FCSTD DOCUMENT  (FreeCAD 0.20R29603 (Git))
Label: DeskAssembly
License: All rights reserved
LicenseURL: http://en.wikipedia.org/wiki/All_rights_reserved
objects: App::Link×17, App::DocumentObjectGroup×3, PartDesign::CoordinateSystem×1, App::FeaturePython×1, App::Part×1
note: 1 computed .brp shape members not serialized (recipe doc carries the construction recipe); baked Part::Feature solids carry a one-line shape summary decoded from their .brp
EXTERNAL_REF file=Desktop.FCStd obj=Model
EXTERNAL_REF file=Parameters.FCStd obj=Spreadsheet
EXTERNAL_REF file=Leg.FCStd obj=Model
EXTERNAL_REF file=LongSkirt.FCStd obj=Model
EXTERNAL_REF file=ShortSkirt.FCStd obj=Model
EXTERNAL_REF file=LegSpacer.FCStd obj=Model

FEATURE [App::DocumentObjectGroup] Parts
FEATURE [PartDesign::CoordinateSystem] LCS_Origin
  AttacherType = Attacher::AttachEngine3D
  MapMode = 2
  Support = -> [X_Axis]
FEATURE [App::DocumentObjectGroup] Constraints
FEATURE [App::FeaturePython] Variables  # WARN: FeaturePython — macro-defined, semantics opaque (R4)
  Type = App::PropertyContainer
FEATURE [App::DocumentObjectGroup] Configurations
FEATURE [App::Link] DeskTop
  AttachedBy = #LCS_Origin
  AttachedTo = Parent Assembly#LCS_Origin
  LinkedObject = -> <external Desktop.FCStd>#Model
FEATURE [App::Link] NorthEastLegA
  AttachedBy = #LCS_Origin
  AttachedTo = Parent Assembly#LCS_Origin
  AttachmentOffset = pos=(0,0,0) rot=(-0.57735,-0.57735,0.57735;4.18879rad)
  LinkPlacement = pos=(-609.6,-286.941,0) rot=(-0.57735,-0.57735,0.57735;4.18879rad)
  LinkedObject = -> <external Leg.FCStd>#Model
  Placement = pos=(-609.6,-286.941,0) rot=(-0.57735,-0.57735,0.57735;4.18879rad)
  expr: .Placement.Base.x = -<<Parameters>>#<<DeskDimensions>>.Skirt_Length / 2
  expr: .Placement.Base.y = -<<Parameters>>#<<DeskDimensions>>.Skirt_Width / 2
FEATURE [App::Link] NorthEastLegB
  AttachedBy = #LCS_Origin
  AttachedTo = Parent Assembly#LCS_Origin
  AttachmentOffset = pos=(0,0,0) rot=(-0.57735,-0.57735,0.57735;4.18879rad)
  LinkPlacement = pos=(-609.6,-310.753,0) rot=(-0.57735,-0.57735,0.57735;4.18879rad)
  LinkedObject = -> <external Leg.FCStd>#Model
  Placement = pos=(-609.6,-310.753,0) rot=(-0.57735,-0.57735,0.57735;4.18879rad)
  expr: .Placement.Base.x = -<<Parameters>>#<<DeskDimensions>>.Skirt_Length / 2
  expr: .Placement.Base.y = -<<Parameters>>#<<DeskDimensions>>.Skirt_Width / 2 - 2 * Parameters#<<DeskDimensions>>.Stock_Thickness
FEATURE [App::Link] NorthWestLegA
  AttachedBy = #LCS_Origin
  AttachedTo = Parent Assembly#LCS_Origin
  AttachmentOffset = pos=(0,0,0) rot=(-0.57735,-0.57735,0.57735;4.18879rad)
  LinkPlacement = pos=(-609.6,298.847,0) rot=(-0.57735,-0.57735,0.57735;4.18879rad)
  LinkedObject = -> <external Leg.FCStd>#Model
  Placement = pos=(-609.6,298.847,0) rot=(-0.57735,-0.57735,0.57735;4.18879rad)
  expr: .Placement.Base.x = -<<Parameters>>#<<DeskDimensions>>.Skirt_Length / 2
  expr: .Placement.Base.y = <<Parameters>>#<<DeskDimensions>>.Skirt_Width / 2 + Parameters#<<DeskDimensions>>.Stock_Thickness
FEATURE [App::Link] NorthWestLegB
  AttachedBy = #LCS_Origin
  AttachedTo = Parent Assembly#LCS_Origin
  AttachmentOffset = pos=(0,0,0) rot=(-0.57735,-0.57735,0.57735;4.18879rad)
  LinkPlacement = pos=(-609.6,322.659,0) rot=(-0.57735,-0.57735,0.57735;4.18879rad)
  LinkedObject = -> <external Leg.FCStd>#Model
  Placement = pos=(-609.6,322.659,0) rot=(-0.57735,-0.57735,0.57735;4.18879rad)
  expr: .Placement.Base.x = -<<Parameters>>#<<DeskDimensions>>.Skirt_Length / 2
  expr: .Placement.Base.y = <<Parameters>>#<<DeskDimensions>>.Skirt_Width / 2 + 3 * Parameters#<<DeskDimensions>>.Stock_Thickness
FEATURE [App::Link] SouthLongSkirt
  AttachedBy = #LCS_Origin
  AttachedTo = Parent Assembly#LCS_Origin
  AttachmentOffset = pos=(0,0,0) rot=(1,0,0;1.5708rad)
  LinkPlacement = pos=(0,310.753,0) rot=(1,0,0;1.5708rad)
  LinkedObject = -> <external LongSkirt.FCStd>#Model
  Placement = pos=(0,310.753,0) rot=(1,0,0;1.5708rad)
  expr: .Placement.Base.y = Parameters#<<DeskDimensions>>.Skirt_Width / 2 + 2 * Parameters#<<DeskDimensions>>.Stock_Thickness
FEATURE [App::Link] NorthLongSkirt
  AttachedBy = #LCS_Origin
  AttachedTo = Parent Assembly#LCS_Origin
  AttachmentOffset = pos=(0,0,0) rot=(1,0,0;1.5708rad)
  LinkPlacement = pos=(0,-298.847,0) rot=(1,0,0;1.5708rad)
  LinkedObject = -> <external LongSkirt.FCStd>#Model
  Placement = pos=(0,-298.847,0) rot=(1,0,0;1.5708rad)
  expr: .Placement.Base.y = -Parameters#<<DeskDimensions>>.Skirt_Width / 2 - Parameters#<<DeskDimensions>>.Stock_Thickness
FEATURE [App::Link] EastShortSkirt
  AttachedBy = #LCS_Origin
  AttachedTo = Parent Assembly#LCS_Origin
  AttachmentOffset = pos=(0,0,0) rot=(-0.57735,0.57735,0.57735;4.18879rad)
  LinkPlacement = pos=(609.6,0,0) rot=(-0.57735,0.57735,0.57735;4.18879rad)
  LinkedObject = -> <external ShortSkirt.FCStd>#Model
  Placement = pos=(609.6,0,0) rot=(-0.57735,0.57735,0.57735;4.18879rad)
  expr: .Placement.Base.x = Parameters#<<DeskDimensions>>.Skirt_Length / 2
FEATURE [App::Link] WestShortSkirt
  AttachedBy = #LCS_Origin
  AttachedTo = Parent Assembly#LCS_Origin
  AttachmentOffset = pos=(0,0,0) rot=(0.57735,0.57735,0.57735;2.0944rad)
  LinkPlacement = pos=(-609.6,0,0) rot=(0.57735,0.57735,0.57735;2.0944rad)
  LinkedObject = -> <external ShortSkirt.FCStd>#Model
  Placement = pos=(-609.6,0,0) rot=(0.57735,0.57735,0.57735;2.0944rad)
  expr: .Placement.Base.x = -Parameters#<<DeskDimensions>>.Skirt_Length / 2
FEATURE [App::Link] SoutEastLegA
  AttachedBy = #LCS_Origin
  AttachedTo = Parent Assembly#LCS_Origin
  AttachmentOffset = pos=(0,0,0) rot=(0.57735,-0.57735,-0.57735;4.18879rad)
  LinkPlacement = pos=(609.6,-298.847,0) rot=(0.57735,-0.57735,-0.57735;4.18879rad)
  LinkedObject = -> <external Leg.FCStd>#Model
  Placement = pos=(609.6,-298.847,0) rot=(0.57735,-0.57735,-0.57735;4.18879rad)
  expr: .Placement.Base.x = <<Parameters>>#<<DeskDimensions>>.Skirt_Length / 2
  expr: .Placement.Base.y = -<<Parameters>>#<<DeskDimensions>>.Skirt_Width / 2 - Parameters#<<DeskDimensions>>.Stock_Thickness
FEATURE [App::Link] SoutEastLegB
  AttachedBy = #LCS_Origin
  AttachedTo = Parent Assembly#LCS_Origin
  AttachmentOffset = pos=(0,0,0) rot=(0.57735,-0.57735,-0.57735;4.18879rad)
  LinkPlacement = pos=(609.6,-322.659,0) rot=(0.57735,-0.57735,-0.57735;4.18879rad)
  LinkedObject = -> <external Leg.FCStd>#Model
  Placement = pos=(609.6,-322.659,0) rot=(0.57735,-0.57735,-0.57735;4.18879rad)
  expr: .Placement.Base.x = <<Parameters>>#<<DeskDimensions>>.Skirt_Length / 2
  expr: .Placement.Base.y = -<<Parameters>>#<<DeskDimensions>>.Skirt_Width / 2 - 3 * Parameters#<<DeskDimensions>>.Stock_Thickness
FEATURE [App::Link] SoutWestLegA
  AttachedBy = #LCS_Origin
  AttachedTo = Parent Assembly#LCS_Origin
  AttachmentOffset = pos=(0,0,0) rot=(0.57735,-0.57735,-0.57735;4.18879rad)
  LinkPlacement = pos=(609.6,310.753,0) rot=(0.57735,-0.57735,-0.57735;4.18879rad)
  LinkedObject = -> <external Leg.FCStd>#Model
  Placement = pos=(609.6,310.753,0) rot=(0.57735,-0.57735,-0.57735;4.18879rad)
  expr: .Placement.Base.x = <<Parameters>>#<<DeskDimensions>>.Skirt_Length / 2
  expr: .Placement.Base.y = <<Parameters>>#<<DeskDimensions>>.Skirt_Width / 2 + 2 * Parameters#<<DeskDimensions>>.Stock_Thickness
FEATURE [App::Link] SoutWestLegB
  AttachedBy = #LCS_Origin
  AttachedTo = Parent Assembly#LCS_Origin
  AttachmentOffset = pos=(0,0,0) rot=(0.57735,-0.57735,-0.57735;4.18879rad)
  LinkPlacement = pos=(609.6,286.941,0) rot=(0.57735,-0.57735,-0.57735;4.18879rad)
  LinkedObject = -> <external Leg.FCStd>#Model
  Placement = pos=(609.6,286.941,0) rot=(0.57735,-0.57735,-0.57735;4.18879rad)
  expr: .Placement.Base.x = <<Parameters>>#<<DeskDimensions>>.Skirt_Length / 2
  expr: .Placement.Base.y = <<Parameters>>#<<DeskDimensions>>.Skirt_Width / 2
FEATURE [App::Link] NorthEastLegSpacer
  AttachedBy = #LCS_Origin
  AttachedTo = Parent Assembly#LCS_Origin
  AttachmentOffset = pos=(0,0,0) rot=(-0.57735,-0.57735,0.57735;4.18879rad)
  LinkPlacement = pos=(-609.6,-298.847,0) rot=(-0.57735,-0.57735,0.57735;4.18879rad)
  LinkedObject = -> <external LegSpacer.FCStd>#Model
  Placement = pos=(-609.6,-298.847,0) rot=(-0.57735,-0.57735,0.57735;4.18879rad)
  expr: .Placement.Base.x = -<<Parameters>>#<<DeskDimensions>>.Skirt_Length / 2
  expr: .Placement.Base.y = -<<Parameters>>#<<DeskDimensions>>.Skirt_Width / 2 - <<Parameters>>#<<DeskDimensions>>.Stock_Thickness
FEATURE [App::Link] NorthWestLegSpacer
  AttachedBy = #LCS_Origin
  AttachedTo = Parent Assembly#LCS_Origin
  AttachmentOffset = pos=(0,0,0) rot=(-0.57735,-0.57735,0.57735;4.18879rad)
  LinkPlacement = pos=(-609.6,310.753,0) rot=(-0.57735,-0.57735,0.57735;4.18879rad)
  LinkedObject = -> <external LegSpacer.FCStd>#Model
  Placement = pos=(-609.6,310.753,0) rot=(-0.57735,-0.57735,0.57735;4.18879rad)
  expr: .Placement.Base.x = -<<Parameters>>#<<DeskDimensions>>.Skirt_Length / 2
  expr: .Placement.Base.y = <<Parameters>>#<<DeskDimensions>>.Skirt_Width / 2 + 2 * Parameters#<<DeskDimensions>>.Stock_Thickness
FEATURE [App::Link] SouthEastLegSpacer
  AttachedBy = #LCS_Origin
  AttachedTo = Parent Assembly#LCS_Origin
  AttachmentOffset = pos=(0,0,0) rot=(0.57735,-0.57735,-0.57735;4.18879rad)
  LinkPlacement = pos=(609.6,-310.753,0) rot=(0.57735,-0.57735,-0.57735;4.18879rad)
  LinkedObject = -> <external LegSpacer.FCStd>#Model
  Placement = pos=(609.6,-310.753,0) rot=(0.57735,-0.57735,-0.57735;4.18879rad)
  expr: .Placement.Base.x = <<Parameters>>#<<DeskDimensions>>.Skirt_Length / 2
  expr: .Placement.Base.y = -<<Parameters>>#<<DeskDimensions>>.Skirt_Width / 2 - 2 * Parameters#<<DeskDimensions>>.Stock_Thickness
FEATURE [App::Link] SouthWestLegSpacer
  AttachedBy = #LCS_Origin
  AttachedTo = Parent Assembly#LCS_Origin
  AttachmentOffset = pos=(0,0,0) rot=(0.57735,-0.57735,-0.57735;4.18879rad)
  LinkPlacement = pos=(609.6,298.847,0) rot=(0.57735,-0.57735,-0.57735;4.18879rad)
  LinkedObject = -> <external LegSpacer.FCStd>#Model
  Placement = pos=(609.6,298.847,0) rot=(0.57735,-0.57735,-0.57735;4.18879rad)
  expr: .Placement.Base.x = <<Parameters>>#<<DeskDimensions>>.Skirt_Length / 2
  expr: .Placement.Base.y = <<Parameters>>#<<DeskDimensions>>.Skirt_Width / 2 + Parameters#<<DeskDimensions>>.Stock_Thickness
FEATURE [App::Part] Model
  AssemblyType = Part::Link
  Group = -> [LCS_Origin,Constraints,Variables,Configurations,DeskTop,NorthEastLegA,NorthEastLegB,NorthWestLegA,NorthWestLegB,SouthLongSkirt,NorthLongSkirt,EastShortSkirt,WestShortSkirt,SoutEastLegA,SoutEastLegB,SoutWestLegA,SoutWestLegB,NorthEastLegSpacer,NorthWestLegSpacer,SouthEastLegSpacer,SouthWestLegSpacer]
  Origin = -> Origin
  Type = Assembly

RESOLVED EXTERNAL PARTS (link-assembly join: the EXTERNAL_REF files above that resolve inside this repo's crawl, each included once):
---- part Desktop.FCStd = doc fcstd_15b475320501 ----
FCSTD DOCUMENT  (FreeCAD 0.20R29603 (Git))
Label: Desktop
License: All rights reserved
LicenseURL: http://en.wikipedia.org/wiki/All_rights_reserved
objects: App::DocumentObjectGroup×3, Sketcher::SketchObject×1, PartDesign::Pad×1, PartDesign::Body×1, PartDesign::CoordinateSystem×1, App::FeaturePython×1, App::Part×1
note: 5 computed .brp shape members not serialized (recipe doc carries the construction recipe); baked Part::Feature solids carry a one-line shape summary decoded from their .brp
EXTERNAL_REF file=Parameters.FCStd obj=Spreadsheet

FEATURE [Sketcher::SketchObject] Sketch
  FullyConstrained = true
  MapMode = 5
  Support = -> [XY_Plane]
  expr: Constraints[8] = <<Parameters>>#<<DeskDimensions>>.Table_Length
  expr: Constraints[9] = <<Parameters>>#<<DeskDimensions>>.Table_Width
  sketch-geometry (4):
    g0: LineSegment StartX=-685.8 StartY=381 StartZ=0 EndX=685.8 EndY=381 EndZ=0
    g1: LineSegment StartX=685.8 StartY=381 StartZ=0 EndX=685.8 EndY=-381 EndZ=0
    g2: LineSegment StartX=685.8 StartY=-381 StartZ=0 EndX=-685.8 EndY=-381 EndZ=0
    g3: LineSegment StartX=-685.8 StartY=-381 StartZ=0 EndX=-685.8 EndY=381 EndZ=0
  constraints (11):
    c: Coincident(g0,g1)
    c: Coincident(g1,g2)
    c: Coincident(g2,g3)
    c: Coincident(g3,g0)
    c: Horizontal(g0)
    c: Horizontal(g2)
    c: Vertical(g1)
    c: Vertical(g3)
    c: DistanceX(g0,g0) = 1371.6
    c: DistanceY(g3,g3) = 762
    c: Symmetric(g0,g1,g-1)
FEATURE [PartDesign::Pad] Pad
  Direction = (0,0,1)
  Length = 11.9062
  Length2 = 10
  Profile = -> Sketch
  ReferenceAxis = -> Sketch [N_Axis]
  Type = 0
  expr: Length = <<Parameters>>#<<DeskDimensions>>.Stock_Thickness
FEATURE [PartDesign::Body] Body
  Group = -> [Sketch,Pad]
  Origin = -> Origin
  Tip = -> Pad
FEATURE [App::DocumentObjectGroup] Parts
FEATURE [PartDesign::CoordinateSystem] LCS_Origin
  AttacherType = Attacher::AttachEngine3D
  MapMode = 2
  Support = -> [X_Axis001]
FEATURE [App::DocumentObjectGroup] Constraints
FEATURE [App::FeaturePython] Variables  # WARN: FeaturePython — macro-defined, semantics opaque (R4)
  Type = App::PropertyContainer
FEATURE [App::DocumentObjectGroup] Configurations
FEATURE [App::Part] Model
  AssemblyType = Part::Link
  Group = -> [LCS_Origin,Constraints,Variables,Configurations,Body]
  Origin = -> Origin001
  SolverId = Asm4EE
  Type = Assembly
---- part Leg.FCStd = doc fcstd_bca13a922b1c ----
FCSTD DOCUMENT  (FreeCAD 0.20R29603 (Git))
Label: Leg
License: All rights reserved
LicenseURL: http://en.wikipedia.org/wiki/All_rights_reserved
objects: App::DocumentObjectGroup×3, Sketcher::SketchObject×1, PartDesign::Pad×1, PartDesign::Body×1, PartDesign::CoordinateSystem×1, App::FeaturePython×1, App::Part×1
note: 5 computed .brp shape members not serialized (recipe doc carries the construction recipe); baked Part::Feature solids carry a one-line shape summary decoded from their .brp
EXTERNAL_REF file=Parameters.FCStd obj=Spreadsheet

FEATURE [Sketcher::SketchObject] Sketch
  FullyConstrained = false
  MapMode = 5
  Support = -> [XY_Plane]
  expr: Constraints[10] = <<Parameters>>#<<DeskDimensions>>.Leg_Top
  expr: Constraints[16] = <<Parameters>>#<<DeskDimensions>>.Leg_Bottom
  expr: Constraints[5] = <<Parameters>>#<<DeskDimensions>>.Leg_Length
  sketch-geometry (8):
    g0: LineSegment StartX=0 StartY=114.3 StartZ=0 EndX=0 EndY=0 EndZ=0
    g1: LineSegment StartX=0 StartY=0 StartZ=0 EndX=762 EndY=-107.092 EndZ=0
    g2: LineSegment StartX=0 StartY=-107.092 StartZ=0 EndX=762 EndY=-107.092 EndZ=0
    g3: LineSegment StartX=762 StartY=-107.092 StartZ=0 EndX=762 EndY=534.568 EndZ=0
    g4: LineSegment StartX=762 StartY=534.568 StartZ=0 EndX=0 EndY=534.568 EndZ=0
    g5: LineSegment StartX=0 StartY=534.568 StartZ=0 EndX=0 EndY=-107.092 EndZ=0
    g6: LineSegment StartX=762 StartY=-107.092 StartZ=0 EndX=762 EndY=-56.2921 EndZ=0
    g7: LineSegment StartX=762 StartY=-56.2921 StartZ=0 EndX=0 EndY=114.3 EndZ=0
  constraints (22):
    c: Coincident(g4,g5)
    c: Coincident(g5,g2)
    c: Horizontal(g4)
    c: Vertical(g3)
    c: Vertical(g5)
    c: DistanceX(g4,g4) = 762
    c: Coincident(g1,g2)
    c: Angle(g1,g0) = 1.71042
    c: Horizontal(g2)
    c: Vertical(g0)
    c: DistanceY(g0,g0) = 114.3
    c: PointOnObject(g0,g5)
    c: Coincident(g6,g1)
    c: Vertical(g6)
    c: Coincident(g7,g6)
    c: Coincident(g7,g0)
    c: DistanceY(g6,g6) = 50.8
    c: Coincident(g3,g1)
    c: Coincident(g4,g3)
    c: Coincident(g1,g0)
    c: DistanceX(g0) = 0
    c: DistanceY(g0) = 0
FEATURE [PartDesign::Pad] Pad
  Direction = (0,0,1)
  Length = 11.9062
  Length2 = 10
  Profile = -> Sketch
  ReferenceAxis = -> Sketch [N_Axis]
  Type = 0
  expr: Length = <<Parameters>>#<<DeskDimensions>>.Stock_Thickness
FEATURE [PartDesign::Body] Body
  Group = -> [Sketch,Pad]
  Origin = -> Origin
  Tip = -> Pad
FEATURE [App::DocumentObjectGroup] Parts
FEATURE [PartDesign::CoordinateSystem] LCS_Origin
  AttacherType = Attacher::AttachEngine3D
  MapMode = 2
  Support = -> [X_Axis001]
FEATURE [App::DocumentObjectGroup] Constraints
FEATURE [App::FeaturePython] Variables  # WARN: FeaturePython — macro-defined, semantics opaque (R4)
  Type = App::PropertyContainer
FEATURE [App::DocumentObjectGroup] Configurations
FEATURE [App::Part] Model
  Group = -> [LCS_Origin,Constraints,Variables,Configurations,Body]
  Origin = -> Origin001
  Type = Assembly
---- part LegSpacer.FCStd = doc fcstd_51fb333a3f8a ----
FCSTD DOCUMENT  (FreeCAD 0.20R29603 (Git))
Label: LegSpacer
License: All rights reserved
LicenseURL: http://en.wikipedia.org/wiki/All_rights_reserved
objects: App::DocumentObjectGroup×3, Sketcher::SketchObject×2, PartDesign::Pad×1, PartDesign::CoordinateSystem×1, App::FeaturePython×1, PartDesign::Pocket×1, PartDesign::Body×1, App::Part×1
note: 8 computed .brp shape members not serialized (recipe doc carries the construction recipe); baked Part::Feature solids carry a one-line shape summary decoded from their .brp
EXTERNAL_REF file=Parameters.FCStd obj=Spreadsheet

FEATURE [Sketcher::SketchObject] Sketch
  FullyConstrained = false
  MapMode = 5
  Support = -> [XY_Plane]
  expr: Constraints[10] = <<Parameters>>#<<DeskDimensions>>.Leg_Top
  expr: Constraints[16] = <<Parameters>>#<<DeskDimensions>>.Leg_Bottom
  expr: Constraints[5] = <<Parameters>>#<<DeskDimensions>>.Leg_Length
  sketch-geometry (8):
    g0: LineSegment StartX=0 StartY=114.3 StartZ=0 EndX=0 EndY=0 EndZ=0
    g1: LineSegment StartX=0 StartY=0 StartZ=0 EndX=762 EndY=-107.092 EndZ=0
    g2: LineSegment StartX=0 StartY=-107.092 StartZ=0 EndX=762 EndY=-107.092 EndZ=0
    g3: LineSegment StartX=762 StartY=-107.092 StartZ=0 EndX=762 EndY=534.568 EndZ=0
    g4: LineSegment StartX=762 StartY=534.568 StartZ=0 EndX=0 EndY=534.568 EndZ=0
    g5: LineSegment StartX=0 StartY=534.568 StartZ=0 EndX=0 EndY=-107.092 EndZ=0
    g6: LineSegment StartX=762 StartY=-107.092 StartZ=0 EndX=762 EndY=-56.2921 EndZ=0
    g7: LineSegment StartX=762 StartY=-56.2921 StartZ=0 EndX=0 EndY=114.3 EndZ=0
  constraints (22):
    c: Coincident(g4,g5)
    c: Coincident(g5,g2)
    c: Horizontal(g4)
    c: Vertical(g3)
    c: Vertical(g5)
    c: DistanceX(g4,g4) = 762
    c: Coincident(g1,g2)
    c: Angle(g1,g0) = 1.71042
    c: Horizontal(g2)
    c: Vertical(g0)
    c: DistanceY(g0,g0) = 114.3
    c: PointOnObject(g0,g5)
    c: Coincident(g6,g1)
    c: Vertical(g6)
    c: Coincident(g7,g6)
    c: Coincident(g7,g0)
    c: DistanceY(g6,g6) = 50.8
    c: Coincident(g3,g1)
    c: Coincident(g4,g3)
    c: Coincident(g1,g0)
    c: DistanceX(g0) = 0
    c: DistanceY(g0) = 0
FEATURE [PartDesign::Pad] Pad
  Direction = (0,0,1)
  Length = 11.9062
  Length2 = 10
  Profile = -> Sketch
  ReferenceAxis = -> Sketch [N_Axis]
  Type = 0
  expr: Length = <<Parameters>>#<<DeskDimensions>>.Stock_Thickness
FEATURE [App::DocumentObjectGroup] Parts
FEATURE [PartDesign::CoordinateSystem] LCS_Origin
  AttacherType = Attacher::AttachEngine3D
  MapMode = 2
  Support = -> [X_Axis001]
FEATURE [App::DocumentObjectGroup] Constraints
FEATURE [App::FeaturePython] Variables  # WARN: FeaturePython — macro-defined, semantics opaque (R4)
  Type = App::PropertyContainer
FEATURE [App::DocumentObjectGroup] Configurations
FEATURE [Sketcher::SketchObject] Sketch001
  AttachmentOffset = pos=(0,0,11.9062) rot=(0,0,1;0rad)
  FullyConstrained = true
  MapMode = 5
  Placement = pos=(0,0,11.9062) rot=(0,0,1;0rad)
  Support = -> [XY_Plane]
  expr: .AttachmentOffset.Base.z = Parameters#<<DeskDimensions>>.Stock_Thickness
  expr: Constraints[8] = Parameters#<<DeskDimensions>>.Leg_Length - 2"
  expr: Constraints[9] = Parameters#<<DeskDimensions>>.Table_Length
  sketch-geometry (4):
    g0: LineSegment StartX=0 StartY=685.8 StartZ=0 EndX=711.2 EndY=685.8 EndZ=0
    g1: LineSegment StartX=711.2 StartY=685.8 StartZ=0 EndX=711.2 EndY=-685.8 EndZ=0
    g2: LineSegment StartX=711.2 StartY=-685.8 StartZ=0 EndX=0 EndY=-685.8 EndZ=0
    g3: LineSegment StartX=0 StartY=-685.8 StartZ=0 EndX=0 EndY=685.8 EndZ=0
  constraints (11):
    c: Coincident(g0,g1)
    c: Coincident(g1,g2)
    c: Coincident(g2,g3)
    c: Coincident(g3,g0)
    c: Horizontal(g0)
    c: Horizontal(g2)
    c: Vertical(g1)
    c: Vertical(g3)
    c: DistanceX(g0,g0) = 711.2
    c: DistanceY(g3,g3) = 1371.6
    c: Symmetric(g2,g0,g-1)
FEATURE [PartDesign::Pocket] Pocket
  BaseFeature = -> Pad
  Direction = (0,0,-1)
  Length = 11.9062
  Length2 = 5
  Profile = -> Sketch001
  ReferenceAxis = -> Sketch001 [N_Axis]
  Type = 0
  expr: Length = Parameters#<<DeskDimensions>>.Stock_Thickness
FEATURE [PartDesign::Body] Body
  Group = -> [Sketch,Pad,Sketch001,Pocket]
  Origin = -> Origin
  Tip = -> Pocket
FEATURE [App::Part] Model
  Group = -> [LCS_Origin,Constraints,Variables,Configurations,Body]
  Origin = -> Origin001
  Type = Assembly
---- part LongSkirt.FCStd = doc fcstd_8dcfb7d38782 ----
FCSTD DOCUMENT  (FreeCAD 0.20R29603 (Git))
Label: LongSkirt
License: All rights reserved
LicenseURL: http://en.wikipedia.org/wiki/All_rights_reserved
objects: App::DocumentObjectGroup×3, Sketcher::SketchObject×1, PartDesign::Pad×1, PartDesign::Body×1, PartDesign::CoordinateSystem×1, App::FeaturePython×1, App::Part×1
note: 5 computed .brp shape members not serialized (recipe doc carries the construction recipe); baked Part::Feature solids carry a one-line shape summary decoded from their .brp
EXTERNAL_REF file=Parameters.FCStd obj=Spreadsheet

FEATURE [Sketcher::SketchObject] Sketch
  FullyConstrained = true
  MapMode = 5
  Support = -> [XY_Plane]
  expr: Constraints[17] = <<Parameters>>#<<DeskDimensions>>.Skirt_Length
  expr: Constraints[18] = <<Parameters>>#<<DeskDimensions>>.Skirt_Height
  expr: Constraints[3] = Parameters#<<DeskDimensions>>.Skirt_Length
  sketch-geometry (8):
    g0: LineSegment StartX=-609.6 StartY=0 StartZ=0 EndX=609.6 EndY=0 EndZ=0
    g1: LineSegment StartX=609.6 StartY=0 StartZ=0 EndX=623.879 EndY=-101.6 EndZ=0
    g2: LineSegment StartX=-623.879 StartY=-101.6 StartZ=0 EndX=-609.6 EndY=0 EndZ=0
    g3: LineSegment StartX=-623.879 StartY=-101.6 StartZ=0 EndX=623.879 EndY=-101.6 EndZ=0
    g4: LineSegment StartX=-609.6 StartY=0 StartZ=0 EndX=609.6 EndY=0 EndZ=0
    g5: LineSegment StartX=609.6 StartY=0 StartZ=0 EndX=609.6 EndY=-101.6 EndZ=0
    g6: LineSegment StartX=609.6 StartY=-101.6 StartZ=0 EndX=-609.6 EndY=-101.6 EndZ=0
    g7: LineSegment StartX=-609.6 StartY=-101.6 StartZ=0 EndX=-609.6 EndY=0 EndZ=0
  constraints (22):
    c: Coincident(g0,g1)
    c: Coincident(g2,g0)
    c: Horizontal(g0)
    c: DistanceX(g0,g0) = 1219.2
    c: Angle(g2,g0) = 1.71042
    c: Angle(g0,g1) = 1.71042
    c: Coincident(g3,g2)
    c: Coincident(g3,g1)
    c: Horizontal(g3)
    c: Coincident(g4,g5)
    c: Coincident(g5,g6)
    c: Coincident(g6,g7)
    c: Coincident(g7,g4)
    c: Horizontal(g4)
    c: Horizontal(g6)
    c: Vertical(g5)
    c: Vertical(g7)
    c: DistanceX(g4,g4) = 1219.2
    c: DistanceY(g5,g5) = 101.6
    c: Coincident(g0,g4)
    c: PointOnObject(g6,g3)
    c: Symmetric(g0,g0,g-1)
FEATURE [PartDesign::Pad] Pad
  Direction = (0,0,1)
  Length = 11.9062
  Length2 = 10
  Profile = -> Sketch
  ReferenceAxis = -> Sketch [N_Axis]
  Type = 0
  expr: Length = Parameters#<<DeskDimensions>>.Stock_Thickness
FEATURE [PartDesign::Body] Body
  Group = -> [Sketch,Pad]
  Origin = -> Origin
  Tip = -> Pad
FEATURE [App::DocumentObjectGroup] Parts
FEATURE [PartDesign::CoordinateSystem] LCS_Origin
  AttacherType = Attacher::AttachEngine3D
  MapMode = 2
  Support = -> [X_Axis001]
FEATURE [App::DocumentObjectGroup] Constraints
FEATURE [App::FeaturePython] Variables  # WARN: FeaturePython — macro-defined, semantics opaque (R4)
  Type = App::PropertyContainer
FEATURE [App::DocumentObjectGroup] Configurations
FEATURE [App::Part] Model
  Group = -> [LCS_Origin,Constraints,Variables,Configurations,Body]
  Origin = -> Origin001
  Type = Assembly
---- part Parameters.FCStd = doc fcstd_c83a1a0fdc62 ----
FCSTD DOCUMENT  (FreeCAD 0.20R29603 (Git))
Label: Parameters
License: All rights reserved
LicenseURL: http://en.wikipedia.org/wiki/All_rights_reserved
objects: Spreadsheet::Sheet×2

FEATURE [Spreadsheet::Sheet] Spreadsheet  label="DeskDimensions"
  cells = A1=Desk Parameters; A2=Stock Thickness; B2(Stock_Thickness)==15" / 32; A4=Table Width; B4(Table_Width)==2.5'; A5=Table Length; B5(Table_Length)==4.5'; A7=Leg Length; B7(Leg_Length)==30"; A8=Leg Top; B8(Leg_Top)==4.5"; A9=Leg Bottom; B9(Leg_Bottom)==2"; A11=Skirt Width; B11(Skirt_Width)==Table_Width - 6" - 3 * Stock_Thickness; A12=Skirt Length; B12(Skirt_Length)==Table_Length - 6"; A13=Skirt Height; B13(Skirt_Height)==4"
FEATURE [Spreadsheet::Sheet] BOM  label="Master BOM"
  cells = A1=ModelName; B1=LeafPart; C1=Quantity; D1=Height; E1=Width; F1=Length; G1=SourceFile; A2=Desktop; B2=1; C2=1; D2=11.90625; E2=1371.6; F2=762; G2=<userpath>/Documents/CAD/SimpleDesk/Desktop.FCStd; A3=Leg; B3=1; C3=8; D3=11.90625; E3=762; F3=221.3921159998366; G3=<userpath>/Documents/CAD/SimpleDesk/Leg.FCStd; A4=LongSkirt; B4=1; C4=2; D4=11.90625; E4=1247.757897611526; F4=101.6; G4=<userpath>/Documents/CAD/SimpleDesk/LongSkirt.FCStd; A5=ShortSkirt; B5=1; C5=2; D5=11.90625; E5=573.88125; F5=101.6; G5=<userpath>/Documents/CAD/SimpleDesk/ShortSkirt.FCStd; A6=LegSpacer; B6=1; C6=4; D6=11.90625; E6=50.79999999999995; F6=62.17280773332241; G6=<userpath>/Documents/CAD/SimpleDesk/LegSpacer.FCStd; A7=DeskAssembly; B7=0; C7=1; D7=773.9062500000001; E7=1433.384231999674; F7=762; G7=<userpath>/Documents/CAD/SimpleDesk/DeskAssembly.FCStd
---- part ShortSkirt.FCStd = doc fcstd_1219c89b2225 ----
FCSTD DOCUMENT  (FreeCAD 0.20R29603 (Git))
Label: ShortSkirt
License: All rights reserved
LicenseURL: http://en.wikipedia.org/wiki/All_rights_reserved
objects: App::DocumentObjectGroup×3, Sketcher::SketchObject×1, PartDesign::Pad×1, PartDesign::Body×1, PartDesign::CoordinateSystem×1, App::FeaturePython×1, App::Part×1
note: 5 computed .brp shape members not serialized (recipe doc carries the construction recipe); baked Part::Feature solids carry a one-line shape summary decoded from their .brp
EXTERNAL_REF file=Parameters.FCStd obj=Spreadsheet

FEATURE [Sketcher::SketchObject] Sketch
  FullyConstrained = true
  MapMode = 5
  Support = -> [XY_Plane]
  expr: Constraints[8] = Parameters#<<DeskDimensions>>.Skirt_Width
  expr: Constraints[9] = Parameters#<<DeskDimensions>>.Skirt_Height
  sketch-geometry (4):
    g0: LineSegment StartX=-286.941 StartY=0 StartZ=0 EndX=286.941 EndY=0 EndZ=0
    g1: LineSegment StartX=286.941 StartY=0 StartZ=0 EndX=286.941 EndY=-101.6 EndZ=0
    g2: LineSegment StartX=286.941 StartY=-101.6 StartZ=0 EndX=-286.941 EndY=-101.6 EndZ=0
    g3: LineSegment StartX=-286.941 StartY=-101.6 StartZ=0 EndX=-286.941 EndY=0 EndZ=0
  constraints (11):
    c: Coincident(g0,g1)
    c: Coincident(g1,g2)
    c: Coincident(g2,g3)
    c: Coincident(g3,g0)
    c: Horizontal(g0)
    c: Horizontal(g2)
    c: Vertical(g1)
    c: Vertical(g3)
    c: DistanceX(g0,g0) = 573.881
    c: DistanceY(g3,g3) = 101.6
    c: Symmetric(g0,g0,g-1)
FEATURE [PartDesign::Pad] Pad
  Direction = (0,0,1)
  Length = 11.9062
  Length2 = 10
  Profile = -> Sketch
  ReferenceAxis = -> Sketch [N_Axis]
  Type = 0
  expr: Length = Parameters#<<DeskDimensions>>.Stock_Thickness
FEATURE [PartDesign::Body] Body
  Group = -> [Sketch,Pad]
  Origin = -> Origin
  Tip = -> Pad
FEATURE [App::DocumentObjectGroup] Parts
FEATURE [PartDesign::CoordinateSystem] LCS_Origin
  AttacherType = Attacher::AttachEngine3D
  MapMode = 2
  Support = -> [X_Axis001]
FEATURE [App::DocumentObjectGroup] Constraints
FEATURE [App::FeaturePython] Variables  # WARN: FeaturePython — macro-defined, semantics opaque (R4)
  Type = App::PropertyContainer
FEATURE [App::DocumentObjectGroup] Configurations
FEATURE [App::Part] Model
  Group = -> [LCS_Origin,Constraints,Variables,Configurations,Body]
  Origin = -> Origin001
  Type = Assembly
